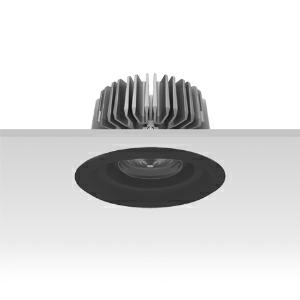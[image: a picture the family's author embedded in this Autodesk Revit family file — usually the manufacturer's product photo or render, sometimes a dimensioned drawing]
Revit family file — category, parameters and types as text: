
# Revit family: 3f_filippi_-_3f_reno_nero_ampio_3f_filippi_-_31267_-_3f_reno_150_bk_3000-840_dali_wide
name_source: partatom
category: Lighting Fixtures
units: mm (PartAtom-declared; Revit-internal decimal feet)

## family parameters
Cut with Voids When Loaded = No
Host = Face
Light Source = No
Part Type = Normal
Room Calculation Point = No
Round Connector Dimension = Use Diameter
Shared = No

## types (1)
- 3F Filippi - 3F Reno Nero Ampio (1 x LED, 2385 lm, 28 W, 4000 K)
    Apparent Load = 28 VA
    Approval mark = CE
    CIE Flux Codes = 82 99 100 100 100
    Color Rendering = 80
    Color Temperature = 4000 K
    Control Gear = Electronic transformer
    Default Elevation = 1800 mm
    Description = ILLUMINOTECHNICAL
Luminous efficiency 100% (DLOR 100%, ULOR 0%).
Initial luminous flux of the luminaire 2385 lm.
Direct symmetric wide distribution.
Installation Interdistance Transv.D = 1.55 x hu - Long.D = 1.55 x hu.
Tabular UGR (CIE 117 - 4H-8H; S=0.25H; 70/50/20): RUG 21.8 - 21.8.
Beam angle: 84° - 83°.
Luminous efficacy 85 lm/W.
Lifetime (L90/B10): 30000 h. (tq+25°C)
Lifetime (L85/B10): 50000 h. (tq+25°C)
Lifetime (L70/B10): 80000 h. (tq+25°C)
Sudden decreased luminous flux after 50000 hours: 0% (C0).
Photobiological safety in compliance with IEC/TR 62778: RG0 risk exempt, (IEC 62471).
In compliance with IEC/EN 62722-2-1 - IEC/EN 62717 standards.

SOURCE
Compact LED module 3000/840.
Energy efficiency class (UE 2019/2020 - UE 2019/2015): E.
CIE 13.3 Colour rendering index: CRI >80 (R9 <50%).
IES TM-30 Fidelity Index: Rf = 84 Rg = 95.
CCT nominal colour temperature 4000 K.
Colour initial tolerance (MacAdam): SDCM 3.
Zhaga Book 3 compliant.

MECHANICAL
Passive heat dissipator in die-casting aluminium, oversized, for optimum thermal management of the LED module.
Parabolic element with graduated/concentric rings in black polycarbonate.
Transparent external lens with glossy and satin differentiated surfaces, with a cooling and anti-insect system in methacrylate (PMMA).
Fastening spring clips in stainless steel.
Dimensions: diameter 166 mm, height 107 mm. Weight 1.28 kg.
IP44 protection degree for exposed part, IP20 for recessed part.
Mechanical strength to impacts IK04 (0.5 joule).
Glow-wire test resistance 650°C.

ELECTRICAL
Wiring on a separate unit.
Halogen Free DALI-2 DATI (Parts 251, 252, 253), PUSH-DIM, electronic wiring 230V-50/60Hz, power factor 0.97 at full load, THD <25%, constant output current, SELV, class II, 1 driver, 1 DALI addresse.
Power of the luminaire 28 W.
ENEC - CE.
SAFE FLICKER: PstLM=<1 and SVM=<0.4 (IEC TR 61547-1 and IEC TR 63158), to ensure a more comfortable and safe light.
Luminaire compliant with EN 60598-2-22 for power supply from a centralised emergency system CPSS (Central Power Supply System), not incorporated in the luminaire - high risk areas excluded. The default power and flux are 100% in AC and 100% in DC.
Ambient temperature from 0°C to +25°C.
Temperature class T6 max 85°C.
Relative humidity UR: <85%.

INSTALLATION
Pull-up recessed fitting.
False ceiling carving: 150 mm.
All accessories dedicated to this product are available on the Catalog and on our website www.3F-Filippi.com.

APPLICATIONS
Environments: architectural, commercial, exhibition areas, transit areas, corridors, shops, display windows, service areas.
In false ceilings with narrow voids.

LIGHT MANAGEMENT
Recommended minimum setting: 10%.
The luminaire, equipped with (DALI-2 DATI) driver, can be controlled manually with 3F Easy Dim technology or automatically/manually with wired or wireless DALI/D2D control systems.
The D2D driver guarantees interoperability with other devices with the same certification by making the following information available:
Device Data (Part 251), Energy Report (Part 252), Diagnosis & Maintenance (Part 253).
In electrical systems without a regulation system (manual or automatic) and DALI bus, a suitable jumper must be made on the DA-DA terminals of the appliance.

WARNING
Luminaire designed for disposal/recycling at end-of-life.
Replaceable (LED only) light source by a professional. Replaceable control gear by a professional.
    Height = 0 mm  [stored 0 ft]
    Lamp = 1 x LED
    Lamp Light Flux = 2385 lm
    Lamp Power = 28 W
    Lamp count = 1
    Length = 166 mm
    Lifetime = 50000 h
    Luminous efficacy = 85 lm/W
    Manufacturer = 3F Filippi
    ModVariant = No
    Model = 3F Filippi - 31267 - 3F Reno 150 BK 3000-840 DALI WIDE
    Mounting Place = Ceiling
    Mounting Type = Recessed
    Number of Poles = 1
    OnlyDefault = Yes
    Power Factor = 1
    Product Name = 3F Filippi - 3F Reno Nero Ampio
    Product group = recessed luminaire
    ProductGroupID = 4
    Protection Class = Protection class II
    Protection Degree = IP 20
    RLX_Detail_Level = 1
    RLX_Emergency_Light_Flux = 0 lm
    RLX_Emergency_Type = 0
    RLX_Emergency_Type_DB = No
    RlxData = <blob elided: 85717 chars, md5=4ab8e490>
    Socket = socket
    Standby Power = 0 W
    System Light Flux = 2385 lm
    System Power = 28 W
    Type Comments = Product without accessories
    Type Image = 3ffilippi_3f_reno_150_ampio_bk_3000_4000.jpg
    URL = http://relux.com
    VarID = ---
    Voltage = 0 V
    Weight = 0.00 kg
    Width = 0 mm  [stored 0 ft]

note: [stored X ft] marks values corroborated as IEEE doubles in the binary element streams (Revit-internal decimal feet)

## geometry (parser evidence)
native form markers: Blend x4, Sweep x11
no freeform markers — native parametric forms only
